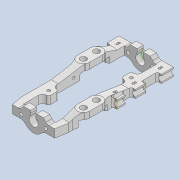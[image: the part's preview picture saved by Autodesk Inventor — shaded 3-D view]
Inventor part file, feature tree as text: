
AUTODESK INVENTOR PART (.ipt)
format: ipt  version: 2020 (Build 240168000, 168)  size: 1,064,960 bytes
history: native  units: mm
features: projected_geometry x29, sketch x26, extrude x24, fillet x12, thicken_offset x10, chamfer x7, other x5, plane x3, reference x3, hole x2
ambient origin geometry x8: Origin, YZ Plane, XZ Plane, XY Plane, X Axis, Y Axis, Z Axis, Center Point
bodies: Solid1 (feature_tree)
feature tree (121):
  extrude  "Extrusion1"  Depth=10.0mm
  plane  "Work Plane1"
  extrude  "Extrusion2"  Depth=2.0mm TaperAngle=0.0deg
  extrude  "Extrusion3"  Depth=10.0mm
  extrude  "Extrusion4"  Depth=2.0mm TaperAngle=0.0deg
  hole  "Hole1"  [1 undecoded]
  thicken_offset  "Thicken1"
  thicken_offset  "Thicken2"
  thicken_offset  "Thicken3"
  thicken_offset  "Thicken4"
  extrude  "Extrusion5"  Depth=54.0mm
  extrude  "Extrusion6"  Depth=2.0mm
  extrude  "Extrusion8"  Depth=2.0mm
  extrude  "Extrusion9"  Depth=2.0mm
  extrude  "Extrusion11"  Depth=3.5mm
  hole  "Hole2"  [1 undecoded]
  extrude  "Extrusion15"  Depth=3.5mm
  extrude  "Extrusion16"  Depth=7.5mm
  chamfer  "Chamfer1"  Distance=2.0mm
  chamfer  "Chamfer2"  Distance=3.25mm
  chamfer  "Chamfer3"  Distance=6.5mm
  chamfer  "Chamfer4"  Distance=6.0mm
  fillet  "Fillet4"  Radius=2.0mm
  fillet  "Fillet5"  Radius=7.0mm
  chamfer  "Chamfer5"  Distance=3.0mm
  fillet  "Fillet6"  Radius=3.0mm
  extrude  "Extrusion17"  Depth=3.0mm
  plane  "Work Plane3"
  extrude  "Extrusion18"  Depth=3.0mm TaperAngle=0.0deg
  plane  "Work Plane4"
  extrude  "Extrusion19"  Depth=3.0mm
  extrude  "Extrusion20"  Depth=3.0mm
  fillet  "Fillet8"  Radius=3.0mm
  fillet  "Fillet9"  Radius=6.0mm
  fillet  "Fillet10"  Radius=2.0mm
  extrude  "Extrusion21"  Depth=3.0mm
  extrude  "Extrusion22"  Depth=2.0mm TaperAngle=0.0deg
  thicken_offset  "Thicken9"
  thicken_offset  "Thicken10"
  thicken_offset  "Thicken11"
  thicken_offset  "Thicken12"
  extrude  "Extrusion23"  Depth=2.0mm TaperAngle=30.0deg
  fillet  "Fillet11"  Radius=5.0mm
  extrude  "Extrusion24"  Depth=2.0mm TaperAngle=30.0deg
  thicken_offset  "Thicken13"
  thicken_offset  "Thicken14"
  chamfer  "Chamfer7"  Distance=5.0mm Angle=30.0deg
  chamfer  "Chamfer8"  Distance=1.0mm
  fillet  "Fillet12"  Radius=8.0mm
  fillet  "Fillet13"  Radius=1.0mm
  fillet  "Fillet14"  Radius=0.5mm
  extrude  "Extrusion25"  Depth=3.0mm
  extrude  "Extrusion26"  Depth=2.0mm
  extrude  "Extrusion27"  Depth=3.0mm
  extrude  "Extrusion28"  Depth=5.0mm TaperAngle=0.0deg
  extrude  "Extrusion29"  Depth=3.0mm
  fillet  "Fillet15"  Radius=5.0mm
  fillet  "Fillet16"  Radius=9.0mm
  sketch  "Sketch1"  dims[d0=10.0mm d1=4.0mm]
  sketch  "Sketch2"  dims[d2=30.0mm d3=2.0mm d4=0.0mm]
  sketch  "Sketch3"  dims[d5=10.0mm d6=4.0mm]
  projected_geometry  "Projected Loop1"
  projected_geometry  "Projected Loop2"
  projected_geometry  "Projected Loop3"
  projected_geometry  "Projected Loop4"
  sketch  "Sketch4"  dims[d7=30.0mm d8=2.0mm d9=0.0mm]
  sketch  "Sketch5"  dims[d10=3.0mm d11=54.0mm]
  sketch  "Sketch6"  dims[d12=3.0mm d13=54.0mm]
  projected_geometry  "Projected Loop5"
  reference  "Reference1"
  reference  "Reference2"
  sketch  "Sketch7"  dims[d14=2.0mm d15=0.0mm d16=4.5mm]
  projected_geometry  "Projected Loop6"
  reference  "Reference3"
  sketch  "Sketch9"  dims[d17=2.0mm d18=0.0mm d19=6.0mm]
  projected_geometry  "Projected Loop9"
  sketch  "Sketch10"  dims[d20=6.0mm]
  projected_geometry  "Projected Loop10"
  sketch  "Sketch12"  dims[d21=1.6mm d22=6.0mm d23=4.0mm d24=2.0mm d25=90.0deg d26=100.0mm d27=0.0mm d28=3.5mm]
  projected_geometry  "Projected Loop13"
  sketch  "Sketch13"  dims[d29=3.5mm d30=3.5mm]
  projected_geometry  "Projected Loop14"
  sketch  "Sketch18"  dims[d31=3.5mm d32=3.5mm]
  projected_geometry  "Projected Loop20"
  sketch  "Sketch19"  dims[d33=3.5mm d34=3.5mm]
  projected_geometry  "Projected Loop21"
  sketch  "Sketch20"  dims[d35=3.5mm d36=7.5mm]
  projected_geometry  "Projected Loop22"
  sketch  "Sketch21"  dims[d37=9.0mm]
  projected_geometry  "Projected Loop23"
  sketch  "Sketch22"  dims[d38=3.0mm]
  projected_geometry  "Projected Loop24"
  sketch  "Sketch23"  dims[d39=3.25mm]
  projected_geometry  "Projected Loop25"
  sketch  "Sketch24"  dims[d40=3.25mm]
  projected_geometry  "Projected Loop26"
  sketch  "Sketch25"  dims[d41=6.0mm]
  projected_geometry  "Projected Loop27"
  sketch  "Sketch26"  dims[d42=6.0mm]
  projected_geometry  "Projected Loop28"
  projected_geometry  "Projected Loop29"
  sketch  "Sketch27"  dims[d43=2.0mm]
  projected_geometry  "Projected Loop30"
  projected_geometry  "Projected Loop31"
  sketch  "Sketch28"  dims[d44=6.5mm]
  projected_geometry  "Projected Loop32"
  sketch  "Sketch29"  dims[d45=6.0mm d46=2.0mm d47=0.0mm]
  projected_geometry  "Projected Loop33"
  sketch  "Sketch30"  dims[d48=7.5mm]
  projected_geometry  "Projected Loop34"
  projected_geometry  "Projected Loop35"
  sketch  "Sketch31"  dims[d49=9.0mm]
  projected_geometry  "Projected Loop36"
  sketch  "Sketch32"  dims[d50=2.0mm d51=3.25mm d52=6.5mm d53=6.0mm d54=2.0mm d55=0.0mm d60=7.0mm d61=3.0mm d62=0.0mm d66=3.0mm d67=3.0mm d68=3.0mm d69=0.0mm d76=6.5mm d77=7.0mm d78=3.0mm d79=0.0mm d80=3.0mm d81=6.0mm d82=4.0mm d83=2.0mm d84=90.0deg d85=100.0mm d86=0.0mm d107=6.0mm d108=2.0mm d109=0.0mm d110=6.0mm d111=2.0mm d112=0.0mm d113=12.0mm d114=2.0mm d115=30.0deg d116=5.0mm d117=2.0mm d118=30.0deg d119=12.0mm d120=2.0mm d121=30.0deg d122=5.0mm d123=2.0mm d124=30.0deg d125=1.0mm d126=8.0mm d127=1.0mm d128=2.0mm d129=30.0deg d130=0.5mm d135=2.5mm d136=2.0mm d137=4.0mm d138=5.0mm d139=0.0mm d140=8.0mm d141=5.0mm d142=0.0mm d143=9.0mm d144=4.0mm d145=0.0mm d146=2.5mm d147=2.0mm d148=4.0mm d149=5.0mm d150=0.0mm d151=1.0mm d152=1.0mm d153=1.0mm d154=3.0mm d155=2.0mm d156=3.0mm d157=2.0mm d158=3.0mm d159=2.0mm d160=0.5mm d161=1.0mm d162=0.5mm d163=1.0mm d164=0.5mm d165=1.0mm d166=8.0mm d167=0.0mm d168=3.0mm d169=0.5mm d170=1.0mm d171=8.0mm d172=0.0mm d173=0.5mm d174=0.5mm d175=0.5mm d176=0.5mm d177=0.5mm d178=0.5mm d179=0.5mm d180=0.5mm d181=12.0mm d182=1.5mm d183=3.0mm d184=5.0mm d185=12.0mm d186=1.5mm d187=3.0mm d188=5.0mm d189=8.0mm d190=0.0mm d191=2.0mm d192=2.5mm d193=1.6mm d194=2.5mm d195=1.6mm d196=8.0mm d197=0.0mm d198=1.0mm d199=1.0mm d200=1.0mm d201=1.0mm d202=1.0mm d203=6.0mm d204=30.0deg d205=1.0mm d206=6.0mm d207=30.0deg d208=4.0mm d209=4.0mm d210=1.0mm d211=1.0mm d212=1.4mm d213=8.0mm d214=0.0mm d215=6.0mm d216=3.0mm d217=10.0mm d218=0.0mm d219=10.0mm d220=0.0mm d221=2.0mm d222=2.0mm d223=10.0mm d224=0.0mm d225=10.0mm d226=0.0mm d227=2.0mm d228=3.0mm]
  projected_geometry  "Projected Loop37"
  projected_geometry  "Projected Loop38"
  parser-record x1  (decoder bookkeeping rows leaked as tree rows — omitted from the tree; the rows remain in map.json)
  other  "tip2_ass_t1.iam"
  other  "cab_coil_1:1"
  other  "cab_coil_1:2"
  other  "bearing_3_6_2:1"
note: 2 required parameter values undecoded (feature->parameter linkage not recoverable at this tier; creation-order binding heuristic only, values carry confidence <= 0.55)
note: 1 file-system path scrubbed to <path> (originals preserved in map.json)
